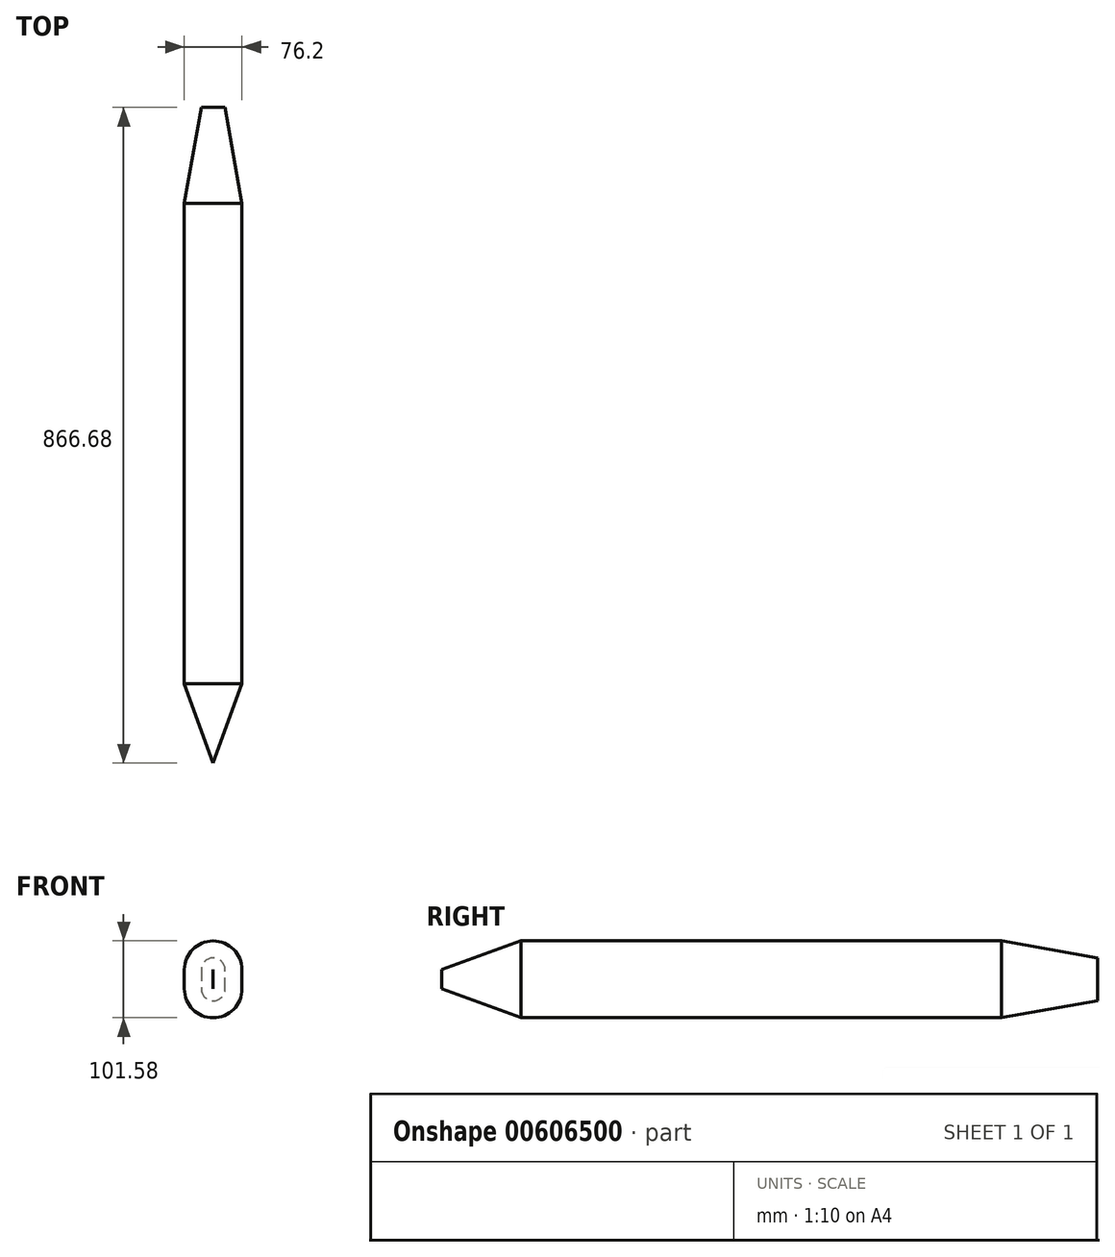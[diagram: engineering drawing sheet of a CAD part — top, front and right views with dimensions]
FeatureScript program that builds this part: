
annotation { "Feature Type Name" : "Feature", "Feature Type Description" : "" }
export const myFeature = defineFeature(function(context is Context, id is Id, definition is map)
    precondition{}
    {
        {
            var Q0;
            Q0=qCreatedBy(makeId("Front.planeOp"),FACE);
            var sketch = newSketch(context, id + "F0", { "sketchPlane" : qUnion([Q0])});
            skLineSegment(sketch, "E0.bottom", {"start": v(38.1, 12.7) * mm, "end": v(-38.1, 12.7) * mm});
            skLineSegment(sketch, "E0.top", {"start": v(38.1, -12.7) * mm, "end": v(-38.1, -12.7) * mm});
            skLineSegment(sketch, "E0.left", {"start": v(38.1, 12.7) * mm, "end": v(38.1, -12.7) * mm});
            skLineSegment(sketch, "E0.right", {"start": v(-38.1, 12.7) * mm, "end": v(-38.1, -12.7) * mm});
            skPoint(sketch, "E0.middle", {"position": v(0, 0) * mm});
            skArc(sketch, "E1", {"start": v(38.1, 12.7) * mm, "mid": v(0, 50.8) * mm, "end": v(-38.1, 12.7) * mm});
            skArc(sketch, "E2", {"start": v(-38.1, -12.7) * mm, "mid": v(0, -50.8) * mm, "end": v(38.1, -12.7) * mm});
            skSolve(sketch);
        }
        {
            var Q0;
            Q0 = qSketchRegion(id + "F0", true);
            extrude(context, id + "F1", {"entities" : qUnion([Q0]), "depth" : 381 * mm, "offsetDistance" : 25.4 * mm, "hasSecondDirection" : true, "secondDirectionOppositeDirection" : true, "secondDirectionDepth" : 254 * mm});
        }
        {
            var Q0;
            Q0=makeQuery(id+"F1.opExtrude","CAP_FACE",FACE,{"disambiguationData":[OSD([sQuery(id+"F0.wireOp",EDGE,"E0.left"),sQuery(id+"F0.wireOp",EDGE,"E0.right"),sQuery(id+"F0.wireOp",EDGE,"E1"),sQuery(id+"F0.wireOp",EDGE,"E2")])],"isStart":false});
            extrude(context, id + "F2", {"entities" : qUnion([Q0]), "operationType" : NewBodyOperationType.ADD, "depth" : 127 * mm, "offsetDistance" : 25.4 * mm, "hasDraft" : true, "draftAngle" : 20 * degree, "draftPullDirection" : true});
        }
        {
            var Q0;
            Q0=makeQuery(id+"F1.opExtrude","CAP_FACE",FACE,{"disambiguationData":[OSD([sQuery(id+"F0.wireOp",EDGE,"E0.left"),sQuery(id+"F0.wireOp",EDGE,"E0.right"),sQuery(id+"F0.wireOp",EDGE,"E1"),sQuery(id+"F0.wireOp",EDGE,"E2")])],"isStart":true});
            extrude(context, id + "F3", {"entities" : qUnion([Q0]), "operationType" : NewBodyOperationType.ADD, "depth" : 127 * mm, "offsetDistance" : 25.4 * mm, "hasDraft" : true, "draftAngle" : 10 * degree, "draftPullDirection" : true});
        }
        {
            var Q0;
            Q0=qCreatedBy(makeId("Top.planeOp"),FACE);
            var sketch = newSketch(context, id + "F4", { "sketchPlane" : qUnion([Q0])});
            skEllipse(sketch, "E3", {"center": v(0, 0) * mm, "majorRadius": 63.59 * mm, "minorRadius": 29.9 * mm, "majorAxis": v(0, -1)});
            skSolve(sketch);
        }
        {
            var Q0;
            Q0=sQuery(id+"F4.wireOp",EDGE,"E3");
            extrude(context, id + "F5", {"bodyType" : ToolBodyType.SURFACE, "surfaceEntities" : qUnion([Q0]), "depth" : 88.9 * mm, "offsetDistance" : 25.4 * mm});
        }
    });
